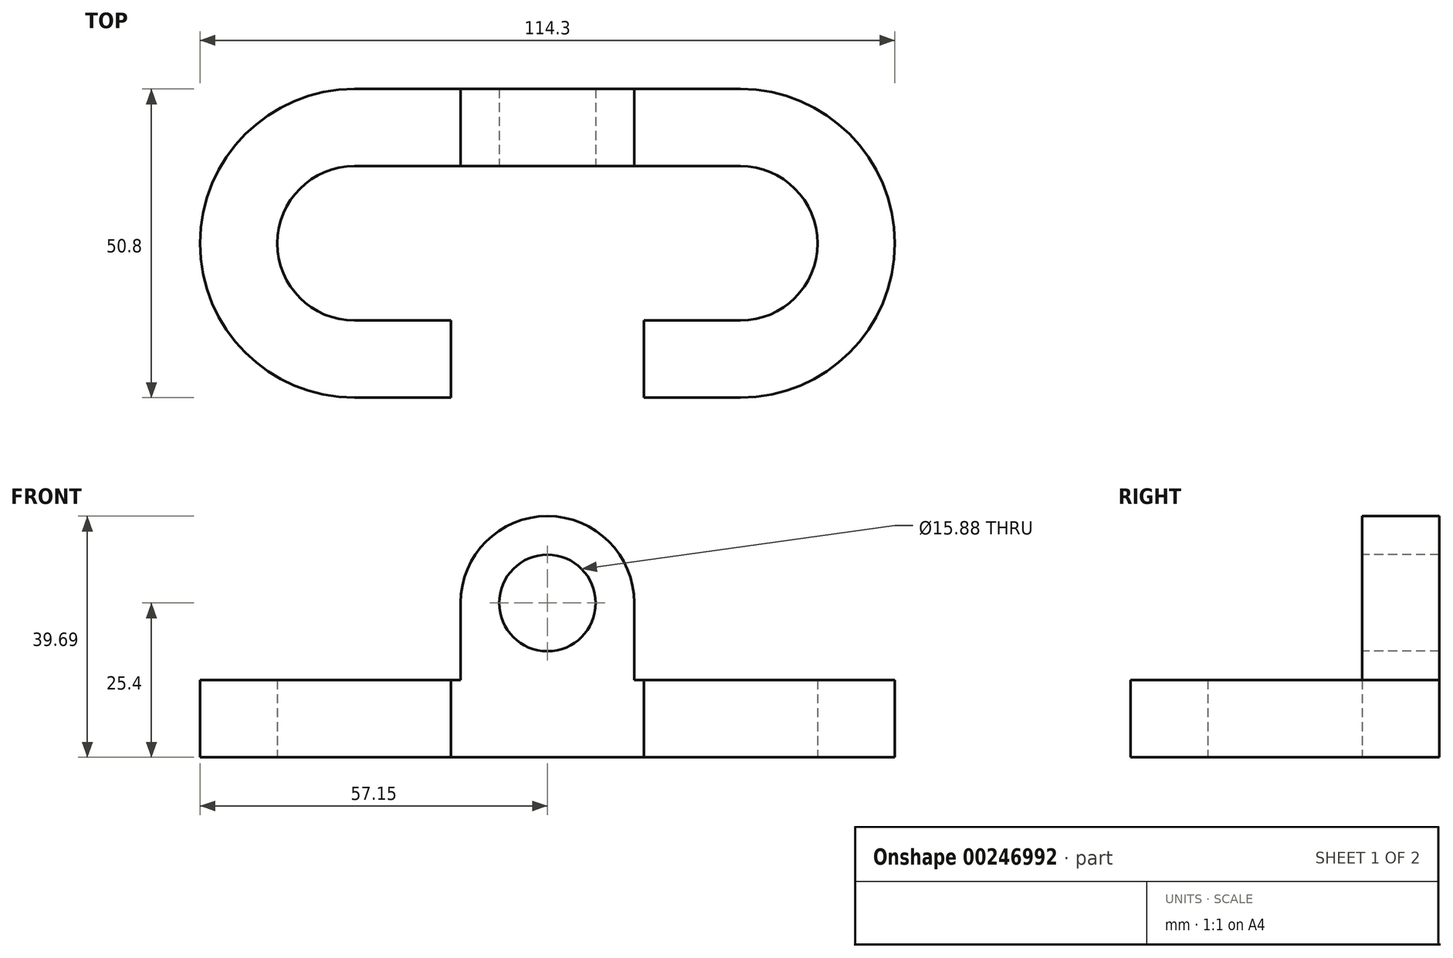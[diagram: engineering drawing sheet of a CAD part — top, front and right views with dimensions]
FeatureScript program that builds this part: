
annotation { "Feature Type Name" : "Feature", "Feature Type Description" : "" }
export const myFeature = defineFeature(function(context is Context, id is Id, definition is map)
    precondition{}
    {
        {
            var Q0;
            Q0=qCreatedBy(makeId("Top.planeOp"),FACE);
            var sketch = newSketch(context, id + "F0", { "sketchPlane" : qUnion([Q0])});
            skArc(sketch, "E0", {"start": v(31.75, -12.7) * mm, "mid": v(44.45, 0) * mm, "end": v(31.75, 12.7) * mm});
            skArc(sketch, "E1", {"start": v(31.75, -25.4) * mm, "mid": v(57.15, 0) * mm, "end": v(31.75, 25.4) * mm});
            skLineSegment(sketch, "E2", {"start": v(31.75, 25.4) * mm, "end": v(0, 25.4) * mm});
            skLineSegment(sketch, "E3", {"start": v(31.75, 12.7) * mm, "end": v(0, 12.7) * mm});
            skLineSegment(sketch, "E4", {"start": v(31.75, -12.7) * mm, "end": v(15.88, -12.7) * mm});
            skLineSegment(sketch, "E5", {"start": v(31.75, 0) * mm, "end": v(31.75, -25.4) * mm});
            skLineSegment(sketch, "E6", {"start": v(31.75, -25.4) * mm, "end": v(15.88, -25.4) * mm});
            skLineSegment(sketch, "E7", {"start": v(15.88, -25.4) * mm, "end": v(15.88, -12.7) * mm});
            skLineSegment(sketch, "E8.MirrorCS", {"start": v(-31.75, 25.4) * mm, "end": v(0, 25.4) * mm});
            skArc(sketch, "E9.MirrorCS", {"start": v(-31.75, -25.4) * mm, "mid": v(-57.15, 0) * mm, "end": v(-31.75, 25.4) * mm});
            skArc(sketch, "E10.MirrorCS", {"start": v(-31.75, -12.7) * mm, "mid": v(-44.45, 0) * mm, "end": v(-31.75, 12.7) * mm});
            skLineSegment(sketch, "E11.MirrorCS", {"start": v(-31.75, -12.7) * mm, "end": v(-15.88, -12.7) * mm});
            skLineSegment(sketch, "E12.MirrorCS", {"start": v(-31.75, -25.4) * mm, "end": v(-15.88, -25.4) * mm});
            skLineSegment(sketch, "E13.MirrorCS", {"start": v(-31.75, 12.7) * mm, "end": v(0, 12.7) * mm});
            skLineSegment(sketch, "E14.MirrorCS", {"start": v(-15.88, -25.4) * mm, "end": v(-15.88, -12.7) * mm});
            skSolve(sketch);
        }
        {
            var Q0;
            Q0 = qSketchRegion(id + "F0", true);
            extrude(context, id + "F1", {"entities" : qUnion([Q0]), "depth" : 12.7 * mm});
        }
        {
            var Q0;
            Q0=makeQuery(id+"F1.opExtrude","SWEPT_FACE",FACE,{"disambiguationData":[OSD([sQuery(id+"F0.wireOp",EDGE,"E3"),sQuery(id+"F0.wireOp",EDGE,"E13.MirrorCS")])]});
            var sketch = newSketch(context, id + "F2", { "sketchPlane" : qUnion([Q0])});
            skCircle(sketch, "E15", {"center": v(0, 25.4) * mm, "radius": 7.94 * mm});
            skPoint(sketch, "E15.centerSnap0", {"position": v(0, 12.7) * mm});
            skArc(sketch, "E16", {"start": v(14.29, 25.4) * mm, "mid": v(0, 39.69) * mm, "end": v(-14.29, 25.4) * mm});
            skLineSegment(sketch, "E17", {"start": v(0, 25.4) * mm, "end": v(-14.29, 25.4) * mm});
            skLineSegment(sketch, "E18", {"start": v(-14.29, 25.4) * mm, "end": v(-14.29, 12.7) * mm});
            skLineSegment(sketch, "E19", {"start": v(0, 25.4) * mm, "end": v(14.29, 25.4) * mm});
            skLineSegment(sketch, "E20", {"start": v(14.29, 25.4) * mm, "end": v(14.29, 12.7) * mm});
            skLineSegment(sketch, "E21", {"start": v(-14.29, 12.7) * mm, "end": v(14.29, 12.7) * mm});
            skSolve(sketch);
        }
        {
            var Q0;
            Q0 = qSketchRegion(id + "F2", true);
            extrude(context, id + "F3", {"entities" : qUnion([Q0]), "operationType" : NewBodyOperationType.ADD, "oppositeDirection" : true, "depth" : 12.7 * mm});
        }
    });
